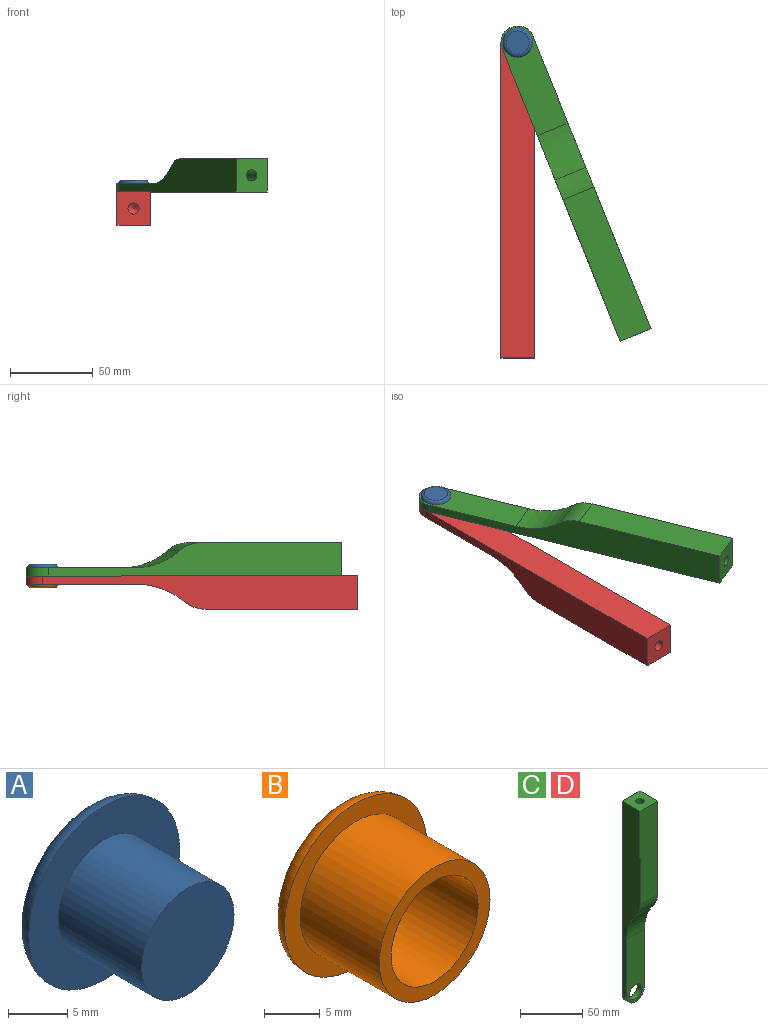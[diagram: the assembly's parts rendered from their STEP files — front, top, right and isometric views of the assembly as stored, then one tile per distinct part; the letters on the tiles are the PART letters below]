
ASSEMBLY  parts=4 mates=3
PART A: 5 faces, bbox 19.5x12x19.5 mm
  f0: plane 14x14mm, normal (0,1,0), area 153.9mm2, adj f1
  f1: torus R=7mm, axis (0,-1,0), area 163.3mm2, adj f0,f3
  f2: cylinder r=5.5mm len=11mm, axis (0,-1,0), area 345.6mm2, adj f3,f4
  f3: plane 18x18mm, normal (0,-1,0), area 159.4mm2, adj f1,f2
  f4: plane 11x11mm, normal (0,-1,0), area 95mm2, adj f2
PART B: 7 faces, bbox 19.5x12x19.5 mm
  f0: plane 14x14mm, normal (0,1,0), area 153.9mm2, adj f6
  f1: cylinder r=7mm len=14mm, axis (0,-1,0), area 439.8mm2, adj f2,f3
  f2: plane 18x18mm, normal (0,-1,0), area 100.5mm2, adj f1,f6
  f3: plane 14x14mm, normal (0,-1,0), area 58.9mm2, adj f1,f4
  f4: cylinder r=5.5mm len=11mm, axis (0,-1,0), area 345.6mm2, adj f3,f5
  f5: plane 11x11mm, normal (0,-1,0), area 95mm2, adj f4
  f6: torus R=7mm, axis (0,-1,0), area 163.3mm2, adj f0,f2
PART C: 12 faces, bbox 20x20x200 mm
  f0: plane 200x20mm, normal (0,1,0), area 3803.1mm2, adj f1,f2,f4,f6,f7
  f1: plane 190x20mm, normal (-1,0,0), area 2597.6mm2, adj f0,f3,f4,f5,f6,f8,f9
  f2: plane 190x20mm, normal (1,0,0), area 2597.6mm2, adj f0,f3,f4,f5,f6,f8,f9
  f3: plane 92.01x20mm, normal (0,-1,0), area 1840.2mm2, adj f1,f2,f4,f9
  f4: plane 20x20mm, normal (0,0,1), area 364.1mm2, adj f0,f1,f2,f3,f10
  f5: plane 66.46x20mm, normal (0,-1,0), area 1132.3mm2, adj f1,f2,f6,f7,f8
  f6: cylinder r=10mm len=20mm, axis (0,-1,0), area 157.1mm2, adj f0,f1,f2,f5
  f7: cylinder r=7mm len=14mm, axis (0,1,0), area 219.9mm2, adj f0,f5
  f8: cylinder r=45mm len=28.75mm, axis (-1,0,0), area 623.8mm2, adj f1,f2,f5,f9
  f9: cylinder r=20mm len=20mm, axis (-1,0,0), area 277.3mm2, adj f1,f2,f3,f8
  f10: cylinder r=3.38mm len=50mm, axis (0,0,1), area 1061.3mm2, adj f4,f11
  f11: cone r=0mm half-angle=59deg, axis (0,0,1), area 41.8mm2, adj f10
PART D: same geometry as C
PLACE A rot(axis=(0.96,0.19,0.19),92.1deg) t=(0,0,12.06)mm
PLACE B rot(axis=(0,-0.71,0.71),180deg) t=(0,0,-2.04)mm
PLACE C rot(axis=(-0.14,0.7,-0.7),164.5deg) t=(5.53,13.02,5)mm
PLACE D rot(axis=(1,0,0),90deg) t=(-10,10,5)mm
MATE slider A.f1 <-> C.f6  axis (0,0,-1) through (0,0,0.06)mm
MATE slider D.f6 <-> B.f1  axis (0,0,-1) through (0,0,0)mm
MATE revolute D.f6 <-> C.f6  axis (0,0,1) through (0,0,5)mm
